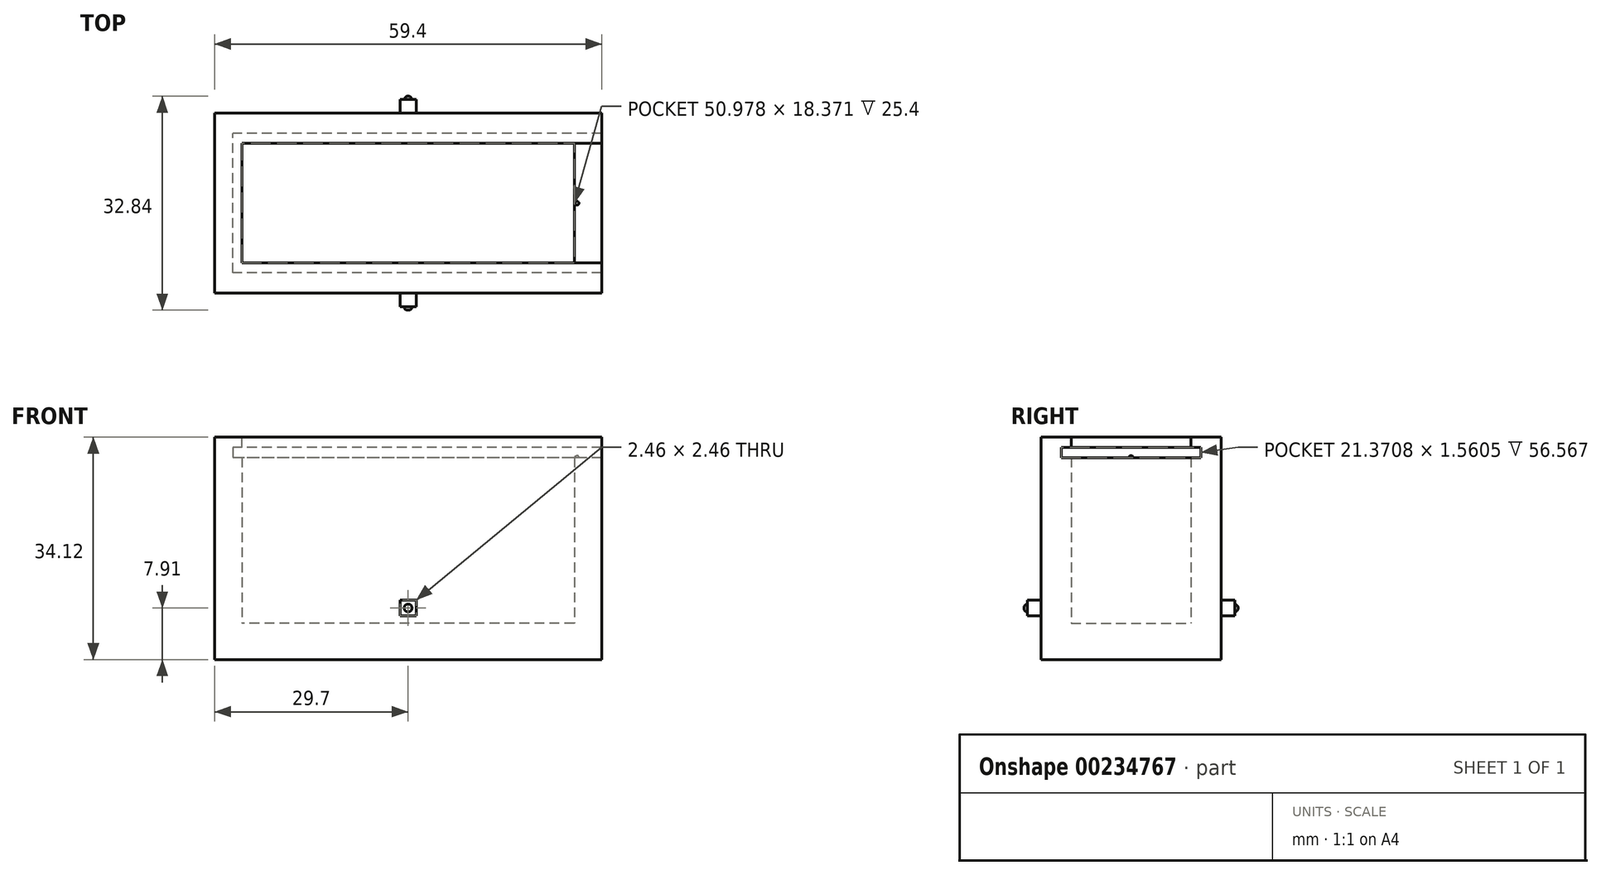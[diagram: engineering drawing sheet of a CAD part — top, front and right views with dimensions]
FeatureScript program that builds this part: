
annotation { "Feature Type Name" : "Feature", "Feature Type Description" : "" }
export const myFeature = defineFeature(function(context is Context, id is Id, definition is map)
    precondition{}
    {
        {
            var Q0;
            Q0=qCreatedBy(makeId("Top.planeOp"),FACE);
            var sketch = newSketch(context, id + "F0", { "sketchPlane" : qUnion([Q0])});
            skLineSegment(sketch, "E0.bottom", {"start": v(29.7, -13.8) * mm, "end": v(-29.7, -13.8) * mm});
            skLineSegment(sketch, "E0.top", {"start": v(29.7, 13.8) * mm, "end": v(-29.7, 13.8) * mm});
            skLineSegment(sketch, "E0.left", {"start": v(29.7, -13.8) * mm, "end": v(29.7, 13.8) * mm});
            skLineSegment(sketch, "E0.right", {"start": v(-29.7, -13.8) * mm, "end": v(-29.7, 13.8) * mm});
            skPoint(sketch, "E0.middle", {"position": v(0, 0) * mm});
            skSolve(sketch);
        }
        {
            var Q0;
            Q0=makeQuery(id+"F0.imprint","IMPRINT",FACE,{"disambiguationData":[TD([[makeQuery(id+"F0.imprint","IMPRINT",EDGE,{"derivedFrom":sQuery(id+"F0.wireOp",EDGE,"E0.bottom")}),-1.0]])]});
            var sketch = newSketch(context, id + "F1", { "sketchPlane" : qUnion([Q0])});
            skLineSegment(sketch, "E1.bottom", {"start": v(25.49, -9.19) * mm, "end": v(-25.49, -9.19) * mm});
            skLineSegment(sketch, "E1.top", {"start": v(25.49, 9.19) * mm, "end": v(-25.49, 9.19) * mm});
            skLineSegment(sketch, "E1.left", {"start": v(25.49, -9.19) * mm, "end": v(25.49, 9.19) * mm});
            skLineSegment(sketch, "E1.right", {"start": v(-25.49, -9.19) * mm, "end": v(-25.49, 9.19) * mm});
            skPoint(sketch, "E1.middle", {"position": v(0, 0) * mm});
            skSolve(sketch);
        }
        {
            var Q0;
            Q0=makeQuery(id+"F1.imprint","IMPRINT",FACE,{"disambiguationData":[TD([[makeQuery(id+"F1.imprint","IMPRINT",EDGE,{"derivedFrom":sQuery(id+"F1.wireOp",EDGE,"E1.bottom")}),1.0]])]});
            extrude(context, id + "F2", {"entities" : qUnion([Q0]), "depth" : 25.4 * mm});
        }
        {
            var Q0;
            Q0=makeQuery(id+"F0.imprint","IMPRINT",FACE,{"disambiguationData":[TD([[makeQuery(id+"F0.imprint","IMPRINT",EDGE,{"derivedFrom":sQuery(id+"F0.wireOp",EDGE,"E0.bottom")}),-1.0]])]});
            extrude(context, id + "F3", {"entities" : qUnion([Q0]), "operationType" : NewBodyOperationType.ADD, "oppositeDirection" : true, "depth" : 5.6 * mm});
        }
        {
            var Q0;
            Q0=makeQuery(id+"F2.opExtrude","CAP_FACE",FACE,{"disambiguationData":[OSD([sQuery(id+"F0.wireOp",EDGE,"E0.bottom"),sQuery(id+"F0.wireOp",EDGE,"E0.top"),sQuery(id+"F0.wireOp",EDGE,"E0.left"),sQuery(id+"F0.wireOp",EDGE,"E0.right"),sQuery(id+"F1.wireOp",EDGE,"E1.bottom"),sQuery(id+"F1.wireOp",EDGE,"E1.top"),sQuery(id+"F1.wireOp",EDGE,"E1.left"),sQuery(id+"F1.wireOp",EDGE,"E1.right")])],"isStart":false});
            var sketch = newSketch(context, id + "F4", { "sketchPlane" : qUnion([Q0])});
            skLineSegment(sketch, "E2.bottom", {"start": v(29.7, -10.69) * mm, "end": v(-26.87, -10.69) * mm});
            skLineSegment(sketch, "E2.top", {"start": v(29.7, 10.69) * mm, "end": v(-26.87, 10.69) * mm});
            skLineSegment(sketch, "E2.left", {"start": v(29.7, -10.69) * mm, "end": v(29.7, 10.69) * mm});
            skLineSegment(sketch, "E2.right", {"start": v(-26.87, -10.69) * mm, "end": v(-26.87, 10.69) * mm});
            skPoint(sketch, "E2.middle", {"position": v(1.41, 0) * mm});
            skPoint(sketch, "E2.middle.positionSnap0", {"position": v(25.49, 0) * mm});
            skPoint(sketch, "E2.centerSnap0", {"position": v(25.49, 0) * mm});
            skSolve(sketch);
        }
        {
            var Q0;
            {var subQ2=sQuery(id+"F4.wireOp",EDGE,"E2.bottom");Q0=makeQuery(id+"F4.imprint","IMPRINT",FACE,{"disambiguationData":[TD([[makeQuery(id+"F4.imprint","IMPRINT",EDGE,{"derivedFrom":subQ2}),1.0]])]});}
            extrude(context, id + "F18", {"entities" : qUnion([Q0]), "operationType" : NewBodyOperationType.ADD, "depth" : 3.12 * mm});
        }
        {
            var Q0;
            Q0=makeQuery(id+"F18.opExtrude","SWEPT_FACE",FACE,{"disambiguationData":[OSD([sQuery(id+"F4.wireOp",EDGE,"E2.right")])]});
            var sketch = newSketch(context, id + "F5", { "sketchPlane" : qUnion([Q0])});
            skLineSegment(sketch, "E3.bottom", {"start": v(-10.69, 28.52) * mm, "end": v(10.69, 28.52) * mm});
            skLineSegment(sketch, "E3.top", {"start": v(-10.69, 26.96) * mm, "end": v(10.69, 26.96) * mm});
            skLineSegment(sketch, "E3.left", {"start": v(-10.69, 28.52) * mm, "end": v(-10.69, 26.96) * mm});
            skLineSegment(sketch, "E3.right", {"start": v(10.69, 28.52) * mm, "end": v(10.69, 26.96) * mm});
            skSolve(sketch);
        }
        {
            var Q0;
            Q0=makeQuery(id+"F18.opExtrude","SWEPT_FACE",FACE,{"disambiguationData":[OSD([sQuery(id+"F4.wireOp",EDGE,"E2.top")])]});
            var sketch = newSketch(context, id + "F6", { "sketchPlane" : qUnion([Q0])});
            skLineSegment(sketch, "E4.bottom", {"start": v(29.7, 26.96) * mm, "end": v(-26.87, 26.96) * mm});
            skLineSegment(sketch, "E4.top", {"start": v(29.7, 28.52) * mm, "end": v(-26.87, 28.52) * mm});
            skLineSegment(sketch, "E4.left", {"start": v(29.7, 26.96) * mm, "end": v(29.7, 28.52) * mm});
            skLineSegment(sketch, "E4.right", {"start": v(-26.87, 26.96) * mm, "end": v(-26.87, 28.52) * mm});
            skSolve(sketch);
        }
        {
            var Q0;
            Q0=makeQuery(id+"F6.imprint","IMPRINT",FACE,{"disambiguationData":[TD([[makeQuery(id+"F6.imprint","IMPRINT",EDGE,{"derivedFrom":sQuery(id+"F6.wireOp",EDGE,"E4.bottom")}),-1.0]])]});
            extrude(context, id + "F7", {"entities" : qUnion([Q0]), "operationType" : NewBodyOperationType.ADD, "depth" : 1.5 * mm});
        }
        {
            var Q0;
            Q0=makeQuery(id+"F18.opExtrude","SWEPT_FACE",FACE,{"disambiguationData":[OSD([sQuery(id+"F4.wireOp",EDGE,"E2.bottom")])]});
            var sketch = newSketch(context, id + "F8", { "sketchPlane" : qUnion([Q0])});
            skLineSegment(sketch, "E5.bottom", {"start": v(-29.7, 26.96) * mm, "end": v(26.87, 26.96) * mm});
            skLineSegment(sketch, "E5.top", {"start": v(-29.7, 28.52) * mm, "end": v(26.87, 28.52) * mm});
            skLineSegment(sketch, "E5.left", {"start": v(-29.7, 26.96) * mm, "end": v(-29.7, 28.52) * mm});
            skLineSegment(sketch, "E5.right", {"start": v(26.87, 26.96) * mm, "end": v(26.87, 28.52) * mm});
            skSolve(sketch);
        }
        {
            var Q0;
            Q0=makeQuery(id+"F8.imprint","IMPRINT",FACE,{"disambiguationData":[TD([[makeQuery(id+"F8.imprint","IMPRINT",EDGE,{"derivedFrom":sQuery(id+"F8.wireOp",EDGE,"E5.bottom")}),1.0]])]});
            extrude(context, id + "F19", {"entities" : qUnion([Q0]), "operationType" : NewBodyOperationType.ADD, "depth" : 1.5 * mm});
        }
        {
            var Q0;
            Q0=makeQuery(id+"F5.imprint","IMPRINT",FACE,{"disambiguationData":[TD([[makeQuery(id+"F5.imprint","IMPRINT",EDGE,{"derivedFrom":sQuery(id+"F5.wireOp",EDGE,"E3.bottom")}),-1.0]])]});
            extrude(context, id + "F9", {"entities" : qUnion([Q0]), "operationType" : NewBodyOperationType.ADD, "depth" : 1.38 * mm});
        }
        {
            var Q0;
            Q0=makeQuery(id+"F2.opExtrude","CAP_FACE",FACE,{"disambiguationData":[OSD([sQuery(id+"F0.wireOp",EDGE,"E0.bottom"),sQuery(id+"F0.wireOp",EDGE,"E0.top"),sQuery(id+"F0.wireOp",EDGE,"E0.left"),sQuery(id+"F0.wireOp",EDGE,"E0.right"),sQuery(id+"F1.wireOp",EDGE,"E1.bottom"),sQuery(id+"F1.wireOp",EDGE,"E1.top"),sQuery(id+"F1.wireOp",EDGE,"E1.left"),sQuery(id+"F1.wireOp",EDGE,"E1.right")])],"isStart":false});
            var sketch = newSketch(context, id + "F20", { "sketchPlane" : qUnion([Q0])});
            skCircle(sketch, "E6", {"center": v(25.9, 0) * mm, "radius": 0.3 * mm});
            skSolve(sketch);
        }
        {
            var Q0;
            Q0=makeQuery(id+"F20.imprint","IMPRINT",FACE,{"disambiguationData":[TD([[makeQuery(id+"F20.imprint","IMPRINT",EDGE,{"derivedFrom":sQuery(id+"F20.wireOp",EDGE,"E6")}),1.0]])]});
            extrude(context, id + "F10", {"entities" : qUnion([Q0]), "operationType" : NewBodyOperationType.ADD, "depth" : 0.3 * mm});
        }
        {
            var Q0;
            Q0=makeQuery(id+"F10.opExtrude","CAP_FACE",FACE,{"disambiguationData":[OSD([sQuery(id+"F20.wireOp",EDGE,"E6")])],"isStart":false});
            fillet(context, id + "F21", {"entities" : qUnion([Q0]), "radius" : 0.25 * mm, "tangentPropagation" : true, "allowEdgeOverflow" : false});
        }
        {
            var Q0;
            {var subQ0=sQuery(id+"F0.wireOp",EDGE,"E0.top");Q0=makeQuery(id+"F18.boolean.opBoolean","MERGE",FACE,{"derivedFrom":[makeQuery(id+"F3.boolean.opBoolean","MERGE",FACE,{"derivedFrom":[makeQuery(id+"F2.opExtrude","SWEPT_FACE",FACE,{"disambiguationData":[OSD([subQ0])]}),makeQuery(id+"F3.opExtrude","SWEPT_FACE",FACE,{"disambiguationData":[OSD([subQ0])]})]}),makeQuery(id+"F18.opExtrude","SWEPT_FACE",FACE,{"disambiguationData":[OSD([subQ0])]})]});}
            var sketch = newSketch(context, id + "F22", { "sketchPlane" : qUnion([Q0])});
            skLineSegment(sketch, "E7.bottom", {"start": v(1.23, 1.1) * mm, "end": v(-1.23, 1.1) * mm});
            skLineSegment(sketch, "E7.top", {"start": v(1.23, 3.5) * mm, "end": v(-1.23, 3.5) * mm});
            skLineSegment(sketch, "E7.left", {"start": v(1.23, 1.1) * mm, "end": v(1.23, 3.5) * mm});
            skLineSegment(sketch, "E7.right", {"start": v(-1.23, 1.1) * mm, "end": v(-1.23, 3.5) * mm});
            skPoint(sketch, "E7.middle", {"position": v(0, 2.3) * mm});
            skSolve(sketch);
        }
        {
            var Q0;
            Q0=makeQuery(id+"F22.imprint","IMPRINT",FACE,{"disambiguationData":[TD([[makeQuery(id+"F22.imprint","IMPRINT",EDGE,{"derivedFrom":sQuery(id+"F22.wireOp",EDGE,"E7.bottom")}),-1.0]])]});
            extrude(context, id + "F11", {"entities" : qUnion([Q0]), "operationType" : NewBodyOperationType.ADD, "depth" : 2.1 * mm});
        }
        {
            var Q0;
            Q0=makeQuery(id+"F11.opExtrude","CAP_FACE",FACE,{"disambiguationData":[OSD([sQuery(id+"F22.wireOp",EDGE,"E7.bottom"),sQuery(id+"F22.wireOp",EDGE,"E7.top"),sQuery(id+"F22.wireOp",EDGE,"E7.left"),sQuery(id+"F22.wireOp",EDGE,"E7.right")])],"isStart":false});
            var sketch = newSketch(context, id + "F12", { "sketchPlane" : qUnion([Q0])});
            skCircle(sketch, "E8", {"center": v(0, 2.3) * mm, "radius": 0.56 * mm});
            skPoint(sketch, "E8.centerSnap0", {"position": v(0, 6.73) * mm});
            skPoint(sketch, "E8.centerSnap1", {"position": v(-1.23, 2.3) * mm});
            skPoint(sketch, "E9", {"position": v(1.23, 2.3) * mm});
            skPoint(sketch, "E10", {"position": v(0, 3.5) * mm});
            skSolve(sketch);
        }
        {
            var Q0;
            Q0=makeQuery(id+"F12.imprint","IMPRINT",FACE,{"disambiguationData":[TD([[makeQuery(id+"F12.imprint","IMPRINT",EDGE,{"derivedFrom":sQuery(id+"F12.wireOp",EDGE,"E8")}),1.0]])]});
            extrude(context, id + "F13", {"entities" : qUnion([Q0]), "operationType" : NewBodyOperationType.ADD, "depth" : 0.5 * mm});
        }
        {
            var Q0;
            Q0=makeQuery(id+"F13.opExtrude","CAP_EDGE",EDGE,{"disambiguationData":[OSD([sQuery(id+"F12.wireOp",EDGE,"E8")])],"isStart":false});
            fillet(context, id + "F14", {"entities" : qUnion([Q0]), "radius" : 0.5 * mm, "tangentPropagation" : true, "allowEdgeOverflow" : false});
        }
        {
            var Q0;
            {var subQ0=sQuery(id+"F0.wireOp",EDGE,"E0.bottom");Q0=makeQuery(id+"F18.boolean.opBoolean","MERGE",FACE,{"derivedFrom":[makeQuery(id+"F3.boolean.opBoolean","MERGE",FACE,{"derivedFrom":[makeQuery(id+"F2.opExtrude","SWEPT_FACE",FACE,{"disambiguationData":[OSD([subQ0])]}),makeQuery(id+"F3.opExtrude","SWEPT_FACE",FACE,{"disambiguationData":[OSD([subQ0])]})]}),makeQuery(id+"F18.opExtrude","SWEPT_FACE",FACE,{"disambiguationData":[OSD([subQ0])]})]});}
            var sketch = newSketch(context, id + "F23", { "sketchPlane" : qUnion([Q0])});
            skLineSegment(sketch, "E11.bottom", {"start": v(1.23, 1.08) * mm, "end": v(-1.23, 1.08) * mm});
            skLineSegment(sketch, "E11.top", {"start": v(1.23, 3.54) * mm, "end": v(-1.23, 3.54) * mm});
            skLineSegment(sketch, "E11.left", {"start": v(1.23, 1.08) * mm, "end": v(1.23, 3.54) * mm});
            skLineSegment(sketch, "E11.right", {"start": v(-1.23, 1.08) * mm, "end": v(-1.23, 3.54) * mm});
            skPoint(sketch, "E11.middle", {"position": v(0, 2.31) * mm});
            skSolve(sketch);
        }
        {
            var Q0;
            Q0=makeQuery(id+"F23.imprint","IMPRINT",FACE,{"disambiguationData":[TD([[makeQuery(id+"F23.imprint","IMPRINT",EDGE,{"derivedFrom":sQuery(id+"F23.wireOp",EDGE,"E11.bottom")}),-1.0]])]});
            extrude(context, id + "F15", {"entities" : qUnion([Q0]), "operationType" : NewBodyOperationType.ADD, "depth" : 2.1 * mm});
        }
        {
            var Q0;
            Q0=makeQuery(id+"F15.opExtrude","CAP_FACE",FACE,{"disambiguationData":[OSD([sQuery(id+"F23.wireOp",EDGE,"E11.bottom"),sQuery(id+"F23.wireOp",EDGE,"E11.top"),sQuery(id+"F23.wireOp",EDGE,"E11.left"),sQuery(id+"F23.wireOp",EDGE,"E11.right")])],"isStart":false});
            var sketch = newSketch(context, id + "F24", { "sketchPlane" : qUnion([Q0])});
            skCircle(sketch, "E12", {"center": v(0, 2.31) * mm, "radius": 0.6 * mm});
            skPoint(sketch, "E12.centerSnap0", {"position": v(1.24, 2.31) * mm});
            skPoint(sketch, "E12.centerSnap1", {"position": v(0, 8.05) * mm});
            skPoint(sketch, "E13", {"position": v(1.23, 2.31) * mm});
            skPoint(sketch, "E14", {"position": v(0, 3.54) * mm});
            skSolve(sketch);
        }
        {
            var Q0;
            Q0=makeQuery(id+"F24.imprint","IMPRINT",FACE,{"disambiguationData":[TD([[makeQuery(id+"F24.imprint","IMPRINT",EDGE,{"derivedFrom":sQuery(id+"F24.wireOp",EDGE,"E12")}),1.0]])]});
            extrude(context, id + "F16", {"entities" : qUnion([Q0]), "operationType" : NewBodyOperationType.ADD, "depth" : 0.5 * mm});
        }
        {
            var Q0;
            Q0=makeQuery(id+"F16.opExtrude","CAP_EDGE",EDGE,{"disambiguationData":[OSD([sQuery(id+"F24.wireOp",EDGE,"E12")])],"isStart":false});
            fillet(context, id + "F17", {"entities" : qUnion([Q0]), "radius" : 0.5 * mm, "tangentPropagation" : true, "allowEdgeOverflow" : false});
        }
    });
